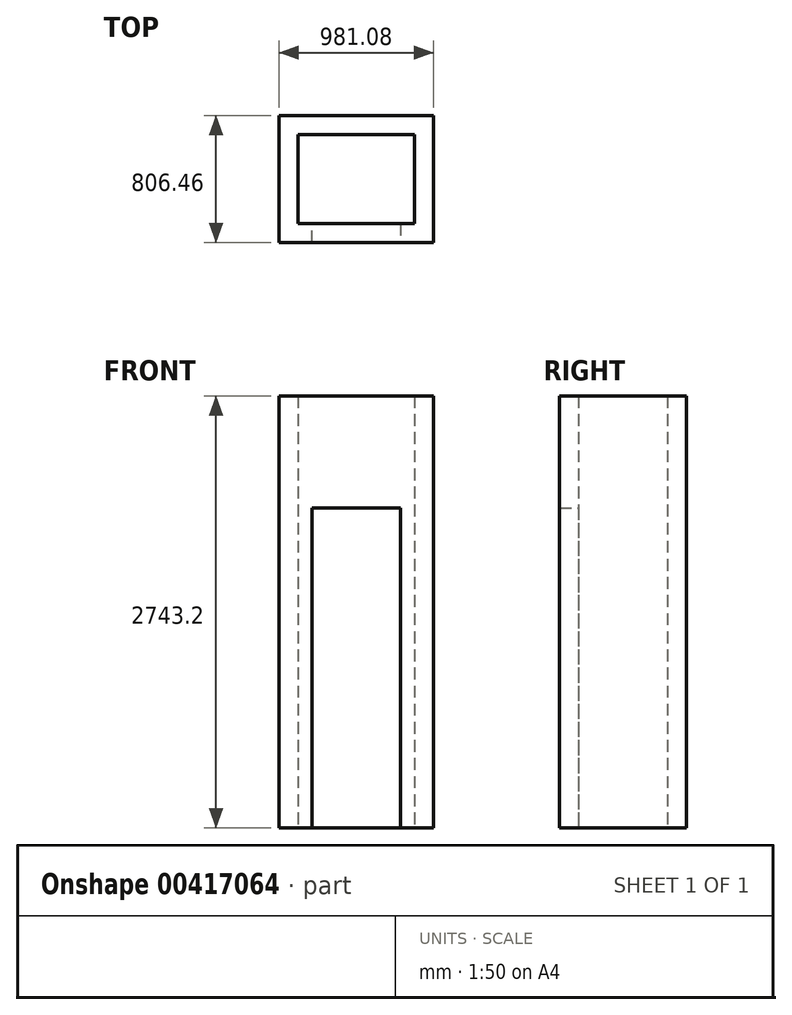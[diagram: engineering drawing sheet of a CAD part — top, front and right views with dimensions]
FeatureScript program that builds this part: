
annotation { "Feature Type Name" : "Feature", "Feature Type Description" : "" }
export const myFeature = defineFeature(function(context is Context, id is Id, definition is map)
    precondition{}
    {
        {
            var Q0;
            Q0=qCreatedBy(makeId("Top.planeOp"),FACE);
            var sketch = newSketch(context, id + "F0", { "sketchPlane" : qUnion([Q0])});
            skLineSegment(sketch, "E0", {"start": v(-280.99, -282.57) * mm, "end": v(-369.89, -282.57) * mm});
            skLineSegment(sketch, "E1", {"start": v(-369.89, -282.58) * mm, "end": v(-369.89, 282.58) * mm});
            skLineSegment(sketch, "E2", {"start": v(-369.89, 282.58) * mm, "end": v(369.89, 282.57) * mm});
            skLineSegment(sketch, "E3", {"start": v(369.89, 282.58) * mm, "end": v(369.89, -282.58) * mm});
            skLineSegment(sketch, "E4", {"start": v(369.89, -282.58) * mm, "end": v(280.99, -282.58) * mm});
            skLineSegment(sketch, "E5", {"start": v(0, 0) * mm, "end": v(0, 282.58) * mm, "construction": true});
            skLineSegment(sketch, "E6", {"start": v(0, 0) * mm, "end": v(-369.89, 0) * mm, "construction": true});
            skLineSegment(sketch, "E7.0", {"start": v(490.54, -403.23) * mm, "end": v(280.99, -403.23) * mm});
            skLineSegment(sketch, "E7.1", {"start": v(-280.99, -403.23) * mm, "end": v(-490.54, -403.23) * mm});
            skLineSegment(sketch, "E7.2", {"start": v(-490.54, -403.22) * mm, "end": v(-490.54, 403.22) * mm});
            skLineSegment(sketch, "E7.3", {"start": v(-490.54, 403.23) * mm, "end": v(490.54, 403.22) * mm});
            skLineSegment(sketch, "E7.4", {"start": v(490.54, 403.22) * mm, "end": v(490.54, -403.22) * mm});
            skLineSegment(sketch, "E8", {"start": v(-280.99, -403.23) * mm, "end": v(-280.99, -282.57) * mm});
            skLineSegment(sketch, "E9", {"start": v(280.99, -282.58) * mm, "end": v(280.99, -403.23) * mm});
            skSolve(sketch);
        }
        {
            var Q0;
            Q0 = qSketchRegion(id + "F0", true);
            extrude(context, id + "F1", {"entities" : qUnion([Q0]), "depth" : 2743.2 * mm});
        }
        {
            var Q0;
            Q0=makeQuery(id+"F1.opExtrude","CAP_FACE",FACE,{"disambiguationData":[OSD([sQuery(id+"F0.wireOp",EDGE,"E0"),sQuery(id+"F0.wireOp",EDGE,"E1"),sQuery(id+"F0.wireOp",EDGE,"E2"),sQuery(id+"F0.wireOp",EDGE,"E3"),sQuery(id+"F0.wireOp",EDGE,"E4"),sQuery(id+"F0.wireOp",EDGE,"E7.0"),sQuery(id+"F0.wireOp",EDGE,"E7.1"),sQuery(id+"F0.wireOp",EDGE,"E7.2"),sQuery(id+"F0.wireOp",EDGE,"E7.3"),sQuery(id+"F0.wireOp",EDGE,"E7.4"),sQuery(id+"F0.wireOp",EDGE,"E8"),sQuery(id+"F0.wireOp",EDGE,"E9")])],"isStart":false});
            var sketch = newSketch(context, id + "F2", { "sketchPlane" : qUnion([Q0])});
            skLineSegment(sketch, "E10.bottom", {"start": v(-280.99, -282.57) * mm, "end": v(280.99, -282.57) * mm});
            skLineSegment(sketch, "E10.top", {"start": v(-280.99, -403.23) * mm, "end": v(280.99, -403.23) * mm});
            skLineSegment(sketch, "E10.left", {"start": v(-280.99, -282.57) * mm, "end": v(-280.99, -403.23) * mm});
            skLineSegment(sketch, "E10.right", {"start": v(280.99, -282.57) * mm, "end": v(280.99, -403.23) * mm});
            skSolve(sketch);
        }
        {
            var Q0;
            Q0 = qSketchRegion(id + "F2", true);
            extrude(context, id + "F3", {"entities" : qUnion([Q0]), "operationType" : NewBodyOperationType.ADD, "oppositeDirection" : true, "depth" : 711.2 * mm});
        }
    });
